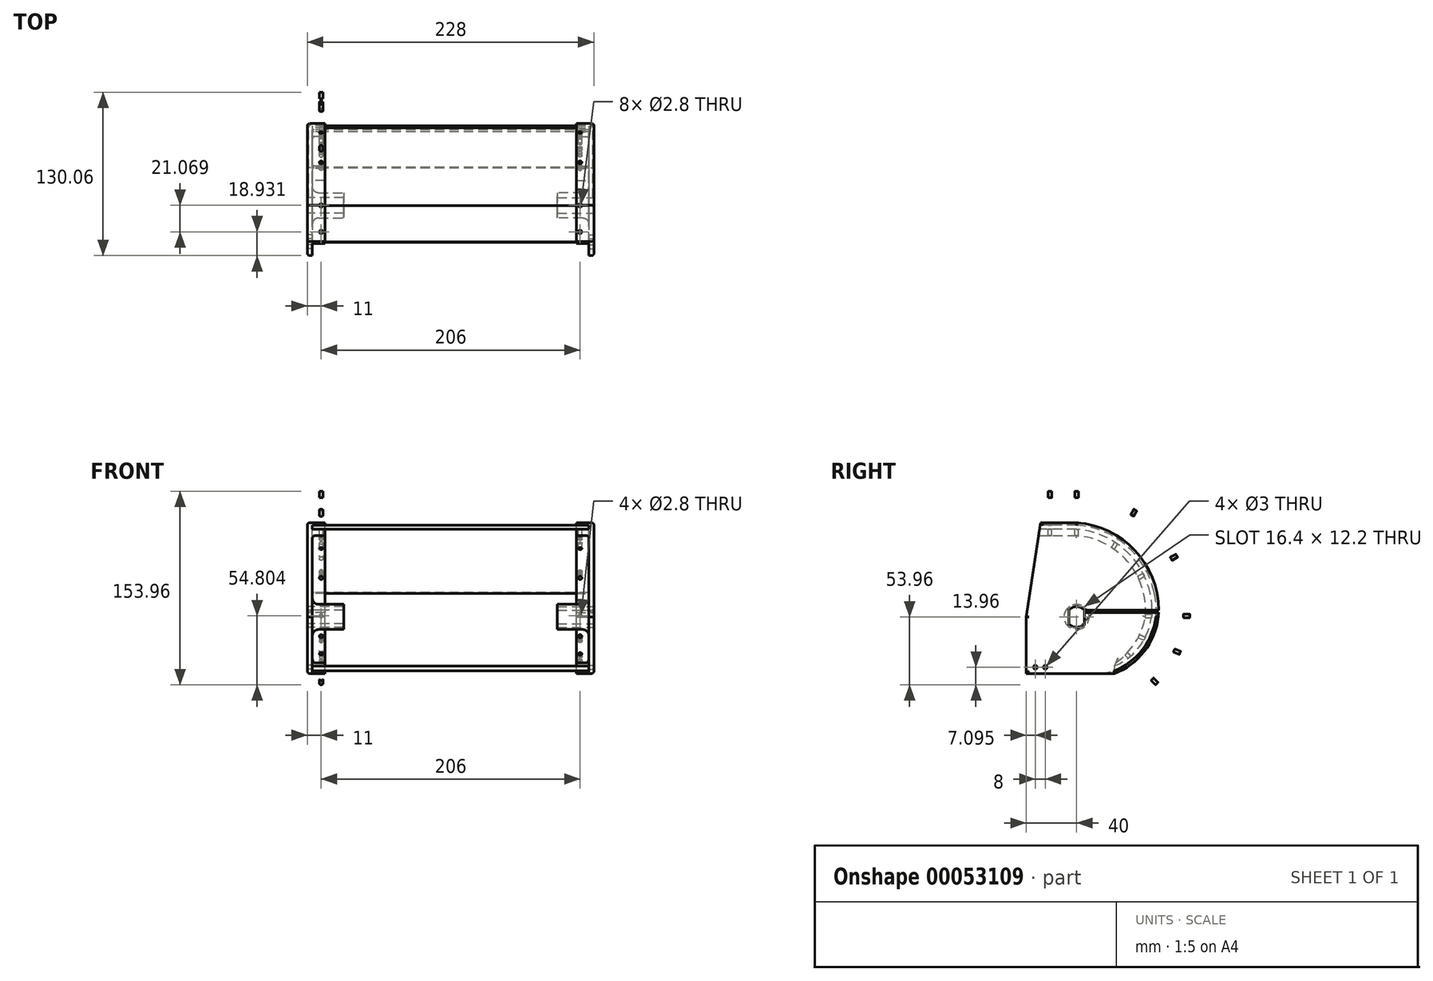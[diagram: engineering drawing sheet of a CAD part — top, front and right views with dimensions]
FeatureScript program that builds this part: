
annotation { "Feature Type Name" : "Feature", "Feature Type Description" : "" }
export const myFeature = defineFeature(function(context is Context, id is Id, definition is map)
    precondition{}
    {
        {
            var Q0;
            Q0=qCreatedBy(makeId("Right.planeOp"),FACE);
            var sketch = newSketch(context, id + "F0", { "sketchPlane" : qUnion([Q0])});
            skCircle(sketch, "E0", {"center": v(0, 0) * mm, "radius": 40 * mm});
            skCircle(sketch, "E1", {"center": v(0, 0) * mm, "radius": 8.2 * mm});
            skLineSegment(sketch, "E2", {"start": v(-6.1, 5.48) * mm, "end": v(-6.1, -5.48) * mm});
            skLineSegment(sketch, "E3", {"start": v(6.1, -5.48) * mm, "end": v(6.1, 5.48) * mm});
            skLineSegment(sketch, "E4", {"start": v(0, 0) * mm, "end": v(0, -45) * mm, "construction": true});
            skLineSegment(sketch, "E5", {"start": v(0, 0) * mm, "end": v(65, 0) * mm, "construction": true});
            skLineSegment(sketch, "E6", {"start": v(0, 0) * mm, "end": v(0, 75) * mm, "construction": true});
            skArc(sketch, "E7", {"start": v(65, 0) * mm, "mid": v(48.17, 51.08) * mm, "end": v(0, 75) * mm});
            skLineSegment(sketch, "E8", {"start": v(0, -45) * mm, "end": v(30, -45) * mm});
            skArc(sketch, "E9", {"start": v(30, -45) * mm, "mid": v(53.79, -27.4) * mm, "end": v(65, 0) * mm});
            skLineSegment(sketch, "E10", {"start": v(0, -45) * mm, "end": v(-40, -45) * mm});
            skLineSegment(sketch, "E11", {"start": v(-40, -45) * mm, "end": v(-40, 0) * mm});
            skLineSegment(sketch, "E12", {"start": v(-28.66, 75) * mm, "end": v(0, 75) * mm});
            skLineSegment(sketch, "E13", {"start": v(-40, 0) * mm, "end": v(-28.66, 75) * mm});
            skLineSegment(sketch, "E14.0", {"start": v(-28.96, 73) * mm, "end": v(-0.07, 73) * mm});
            skArc(sketch, "E14.1", {"start": v(61.76, 19.33) * mm, "mid": v(39.87, 56.56) * mm, "end": v(-0.07, 73) * mm});
            skArc(sketch, "E14.2", {"start": v(29.5, -43.05) * mm, "mid": v(57.45, -17.97) * mm, "end": v(61.76, 19.33) * mm});
            skArc(sketch, "E15.0", {"start": v(20.83, -42.2) * mm, "mid": v(52.6, -19.83) * mm, "end": v(58.54, 18.58) * mm});
            skArc(sketch, "E15.1", {"start": v(58.54, 18.58) * mm, "mid": v(37.77, 54) * mm, "end": v(-0.18, 69.7) * mm});
            skLineSegment(sketch, "E15.2", {"start": v(-29.46, 69.7) * mm, "end": v(-0.18, 69.7) * mm});
            skArc(sketch, "E16.1", {"start": v(54.69, 0.26) * mm, "mid": v(40.66, 44) * mm, "end": v(-0.35, 64.7) * mm});
            skLineSegment(sketch, "E16.2", {"start": v(-30.22, 64.7) * mm, "end": v(-0.35, 64.7) * mm});
            skLineSegment(sketch, "E17", {"start": v(29.5, -43.05) * mm, "end": v(19.71, -45) * mm});
            skLineSegment(sketch, "E18", {"start": v(20.86, -42.37) * mm, "end": v(20.83, -42.2) * mm});
            skArc(sketch, "E19", {"start": v(20.86, -42.37) * mm, "mid": v(43.09, -25.27) * mm, "end": v(54.69, 0.26) * mm});
            skLineSegment(sketch, "E20", {"start": v(30.2, -39.2) * mm, "end": v(31.32, -36.44) * mm});
            skPoint(sketch, "E21", {"position": v(-32.9, -40) * mm});
            skPoint(sketch, "E22", {"position": v(-24.9, -40) * mm});
            skCircle(sketch, "E23", {"center": v(-32.9, -40) * mm, "radius": 1.5 * mm});
            skCircle(sketch, "E24", {"center": v(-24.9, -40) * mm, "radius": 1.5 * mm});
            skSolve(sketch);
        }
        {
            var Q0;
            Q0=makeQuery(id+"F0.imprint","IMPRINT",FACE,{"disambiguationData":[TD([[makeQuery(id+"F0.imprint","IMPRINT",EDGE,{"derivedFrom":sQuery(id+"F0.wireOp",EDGE,"E7")}),1.0]])]});
            var Q1;
            {var subQ4=sQuery(id+"F0.wireOp",EDGE,"E1");var subQ8=sQuery(id+"F0.wireOp",EDGE,"E2");var subQ9=makeQuery(id+"F0.imprint","INTERSECT",VERTEX,{"disambiguationData":[OD(0.0)],"derivedFrom":[subQ4,subQ8]});Q1=makeQuery(id+"F0.imprint","IMPRINT",FACE,{"disambiguationData":[TD([[makeQuery(id+"F0.imprint","IMPRINT",EDGE,{"disambiguationData":[TD([[subQ9,1.0]])],"derivedFrom":subQ4}),-1.0]])]});}
            var Q2;
            {var subQ0=sQuery(id+"F0.wireOp",EDGE,"E2");Q2=makeQuery(id+"F0.imprint","IMPRINT",FACE,{"disambiguationData":[TD([[makeQuery(id+"F0.imprint","IMPRINT",EDGE,{"derivedFrom":subQ0}),-1.0]])]});}
            var Q3;
            {var subQ0=sQuery(id+"F0.wireOp",EDGE,"E3");Q3=makeQuery(id+"F0.imprint","IMPRINT",FACE,{"disambiguationData":[TD([[makeQuery(id+"F0.imprint","IMPRINT",EDGE,{"derivedFrom":subQ0}),-1.0]])]});}
            var Q4;
            {var subQ12=sQuery(id+"F0.wireOp",EDGE,"E10");Q4=makeQuery(id+"F0.imprint","IMPRINT",FACE,{"disambiguationData":[TD([[makeQuery(id+"F0.imprint","IMPRINT",EDGE,{"derivedFrom":subQ12}),-1.0]])]});}
            var Q5;
            {var subQ4=sQuery(id+"F0.wireOp",EDGE,"E15.0");Q5=makeQuery(id+"F0.imprint","IMPRINT",FACE,{"disambiguationData":[TD([[makeQuery(id+"F0.imprint","IMPRINT",EDGE,{"derivedFrom":subQ4}),1.0]])]});}
            var Q6;
            {var subQ4=sQuery(id+"F0.wireOp",EDGE,"E14.0");Q6=makeQuery(id+"F0.imprint","IMPRINT",FACE,{"disambiguationData":[TD([[makeQuery(id+"F0.imprint","IMPRINT",EDGE,{"derivedFrom":subQ4}),-1.0]])]});}
            var Q7;
            {var subQ0=sQuery(id+"F0.wireOp",EDGE,"E18");Q7=makeQuery(id+"F0.imprint","IMPRINT",FACE,{"disambiguationData":[TD([[makeQuery(id+"F0.imprint","IMPRINT",EDGE,{"derivedFrom":subQ0}),1.0]])]});}
            var Q8;
            {var subQ7=sQuery(id+"F0.wireOp",EDGE,"E15.1");Q8=makeQuery(id+"F0.imprint","IMPRINT",FACE,{"disambiguationData":[TD([[makeQuery(id+"F0.imprint","IMPRINT",EDGE,{"derivedFrom":subQ7}),1.0]])]});}
            var Q9;
            {var subQ0=sQuery(id+"F0.wireOp",EDGE,"E18");Q9=makeQuery(id+"F0.imprint","IMPRINT",FACE,{"disambiguationData":[TD([[makeQuery(id+"F0.imprint","IMPRINT",EDGE,{"derivedFrom":subQ0}),-1.0]])]});}
            var Q10;
            Q10=sQuery(id+"F0.wireOp",EDGE,"E12");
            var Q11;
            Q11=sQuery(id+"F0.wireOp",EDGE,"E13");
            var Q12;
            Q12=sQuery(id+"F0.wireOp",EDGE,"E11");
            var Q13;
            Q13=sQuery(id+"F0.wireOp",EDGE,"E10");
            var Q14;
            Q14=sQuery(id+"F0.wireOp",EDGE,"E8");
            var Q15;
            Q15=sQuery(id+"F0.wireOp",EDGE,"E9");
            var Q16;
            Q16=sQuery(id+"F0.wireOp",EDGE,"E7");
            extrude(context, id + "F1", {"entities" : qUnion([Q0, Q1, Q2, Q3, Q4, Q5, Q6, Q7, Q8, Q9]), "surfaceEntities" : qUnion([Q10, Q11, Q12, Q13, Q14, Q15, Q16]), "depth" : 29 * mm});
        }
        {
            var Q0;
            Q0=makeQuery(id+"F1.opExtrude","CAP_FACE",FACE,{"disambiguationData":[OSD([sQuery(id+"F0.wireOp",EDGE,"E1"),sQuery(id+"F0.wireOp",EDGE,"E2"),sQuery(id+"F0.wireOp",EDGE,"E3"),sQuery(id+"F0.wireOp",EDGE,"E7"),sQuery(id+"F0.wireOp",EDGE,"E8"),sQuery(id+"F0.wireOp",EDGE,"E9"),sQuery(id+"F0.wireOp",EDGE,"E10"),sQuery(id+"F0.wireOp",EDGE,"E11"),sQuery(id+"F0.wireOp",EDGE,"E12"),sQuery(id+"F0.wireOp",EDGE,"E13"),sQuery(id+"F0.wireOp",EDGE,"b91848d7-33e1-4d5c-aaae-2f8c404cd7a8"),sQuery(id+"F0.wireOp",EDGE,"291409aa-1abd-44d4-8dab-fd7a7754a467")])],"isStart":false});
            var sketch = newSketch(context, id + "F2", { "sketchPlane" : qUnion([Q0])});
            skCircle(sketch, "E25", {"center": v(0, 0) * mm, "radius": 10 * mm});
            skSolve(sketch);
        }
        {
            var Q0;
            {var subQ1=sQuery(id+"F0.wireOp",EDGE,"E2");Q0=makeQuery(id+"F2.imprint","IMPRINT",FACE,{"disambiguationData":[TD([[makeQuery(id+"F2.imprint","IMPRINT",EDGE,{"derivedFrom":makeQuery(id+"F1.opExtrude","CAP_EDGE",EDGE,{"disambiguationData":[OSD([subQ1])],"isStart":true})}),-1.0]])]});}
            var Q1;
            Q1=makeQuery(id+"F2.imprint","IMPRINT",FACE,{"disambiguationData":[TD([[makeQuery(id+"F2.imprint","IMPRINT",EDGE,{"derivedFrom":sQuery(id+"F2.wireOp",EDGE,"E25")}),-1.0]])]});
            extrude(context, id + "F3", {"entities" : qUnion([Q0, Q1]), "operationType" : NewBodyOperationType.REMOVE, "oppositeDirection" : true, "depth" : 25 * mm});
        }
        {
            var Q0;
            {var subQ7=sQuery(id+"F0.wireOp",EDGE,"E15.1");Q0=makeQuery(id+"F0.imprint","IMPRINT",FACE,{"disambiguationData":[TD([[makeQuery(id+"F0.imprint","IMPRINT",EDGE,{"derivedFrom":subQ7}),1.0]])]});}
            extrude(context, id + "F4", {"entities" : qUnion([Q0]), "operationType" : NewBodyOperationType.ADD, "depth" : 10 * mm});
        }
        {
            var Q0;
            Q0=makeQuery(id+"F0.imprint","IMPRINT",FACE,{"disambiguationData":[TD([[makeQuery(id+"F0.imprint","IMPRINT",EDGE,{"derivedFrom":sQuery(id+"F0.wireOp",EDGE,"E7")}),1.0]])]});
            extrude(context, id + "F5", {"entities" : qUnion([Q0]), "operationType" : NewBodyOperationType.ADD, "depth" : 10 * mm});
        }
        {
            var Q0;
            Q0=makeQuery(id+"F3.boolean.opBoolean","COPY",EDGE,{"derivedFrom":makeQuery(id+"F3.opExtrude","CAP_EDGE",EDGE,{"disambiguationData":[OSD([sQuery(id+"F2.wireOp",EDGE,"E25")])],"isStart":false})});
            fillet(context, id + "F6", {"entities" : qUnion([Q0]), "radius" : 5 * mm, "tangentPropagation" : true, "allowEdgeOverflow" : false});
        }
        {
            var Q0;
            Q0=makeQuery(id+"F3.boolean.opBoolean","COPY",EDGE,{"derivedFrom":makeQuery(id+"F3.opExtrude","CAP_EDGE",EDGE,{"disambiguationData":[OSD([sQuery(id+"F2.wireOp",EDGE,"E25")])],"isStart":true})});
            var Q1;
            Q1=makeQuery(id+"F4.boolean.opBoolean","INTERSECT",EDGE,{"derivedFrom":[makeQuery(id+"F3.boolean.opBoolean","COPY",FACE,{"derivedFrom":makeQuery(id+"F3.opExtrude","CAP_FACE",FACE,{"disambiguationData":[OSD([sQuery(id+"F0.wireOp",EDGE,"E7"),sQuery(id+"F0.wireOp",EDGE,"E8"),sQuery(id+"F0.wireOp",EDGE,"E9"),sQuery(id+"F0.wireOp",EDGE,"E10"),sQuery(id+"F0.wireOp",EDGE,"E11"),sQuery(id+"F0.wireOp",EDGE,"E12"),sQuery(id+"F0.wireOp",EDGE,"E13"),sQuery(id+"F2.wireOp",EDGE,"E25")])],"isStart":false})}),makeQuery(id+"F4.opExtrude","SWEPT_FACE",FACE,{"disambiguationData":[OSD([sQuery(id+"F0.wireOp",EDGE,"E19")])]})]});
            var Q2;
            Q2=makeQuery(id+"F4.boolean.opBoolean","INTERSECT",EDGE,{"derivedFrom":[makeQuery(id+"F3.boolean.opBoolean","COPY",FACE,{"derivedFrom":makeQuery(id+"F3.opExtrude","CAP_FACE",FACE,{"disambiguationData":[OSD([sQuery(id+"F0.wireOp",EDGE,"E7"),sQuery(id+"F0.wireOp",EDGE,"E8"),sQuery(id+"F0.wireOp",EDGE,"E9"),sQuery(id+"F0.wireOp",EDGE,"E10"),sQuery(id+"F0.wireOp",EDGE,"E11"),sQuery(id+"F0.wireOp",EDGE,"E12"),sQuery(id+"F0.wireOp",EDGE,"E13"),sQuery(id+"F2.wireOp",EDGE,"E25")])],"isStart":false})}),makeQuery(id+"F4.opExtrude","SWEPT_FACE",FACE,{"disambiguationData":[OSD([sQuery(id+"F0.wireOp",EDGE,"E16.1")])]})]});
            var Q3;
            Q3=makeQuery(id+"F4.boolean.opBoolean","INTERSECT",EDGE,{"derivedFrom":[makeQuery(id+"F3.boolean.opBoolean","COPY",FACE,{"derivedFrom":makeQuery(id+"F3.opExtrude","CAP_FACE",FACE,{"disambiguationData":[OSD([sQuery(id+"F0.wireOp",EDGE,"E7"),sQuery(id+"F0.wireOp",EDGE,"E8"),sQuery(id+"F0.wireOp",EDGE,"E9"),sQuery(id+"F0.wireOp",EDGE,"E10"),sQuery(id+"F0.wireOp",EDGE,"E11"),sQuery(id+"F0.wireOp",EDGE,"E12"),sQuery(id+"F0.wireOp",EDGE,"E13"),sQuery(id+"F2.wireOp",EDGE,"E25")])],"isStart":false})}),makeQuery(id+"F4.opExtrude","SWEPT_FACE",FACE,{"disambiguationData":[OSD([sQuery(id+"F0.wireOp",EDGE,"E16.2")])]})]});
            var Q4;
            {var subQ0=sQuery(id+"F0.wireOp",EDGE,"E13");var subQ1=sQuery(id+"F0.wireOp",EDGE,"E11");Q4=makeQuery(id+"F4.boolean.opBoolean","SPLIT",EDGE,{"disambiguationData":[TD([makeQuery(id+"F1.opExtrude","SWEPT_FACE",FACE,{"disambiguationData":[OSD([subQ1])]})])],"derivedFrom":makeQuery(id+"F3.boolean.opBoolean","COPY",EDGE,{"derivedFrom":makeQuery(id+"F3.opExtrude","CAP_EDGE",EDGE,{"disambiguationData":[OSD([subQ0])],"isStart":false})})});}
            var Q5;
            Q5=makeQuery(id+"F3.boolean.opBoolean","COPY",EDGE,{"derivedFrom":makeQuery(id+"F3.opExtrude","CAP_EDGE",EDGE,{"disambiguationData":[OSD([sQuery(id+"F0.wireOp",EDGE,"E11")])],"isStart":false})});
            var Q6;
            Q6=makeQuery(id+"F3.boolean.opBoolean","COPY",EDGE,{"derivedFrom":makeQuery(id+"F3.opExtrude","CAP_EDGE",EDGE,{"disambiguationData":[OSD([sQuery(id+"F0.wireOp",EDGE,"E8"),sQuery(id+"F0.wireOp",EDGE,"E10")])],"isStart":false})});
            var Q7;
            Q7=makeQuery(id+"F1.opExtrude","CAP_EDGE",EDGE,{"disambiguationData":[OSD([sQuery(id+"F0.wireOp",EDGE,"E11")])],"isStart":true});
            var Q8;
            Q8=makeQuery(id+"F1.opExtrude","CAP_EDGE",EDGE,{"disambiguationData":[OSD([sQuery(id+"F0.wireOp",EDGE,"E13")])],"isStart":true});
            var Q9;
            Q9=makeQuery(id+"F1.opExtrude","CAP_EDGE",EDGE,{"disambiguationData":[OSD([sQuery(id+"F0.wireOp",EDGE,"E8"),sQuery(id+"F0.wireOp",EDGE,"E10")])],"isStart":true});
            var Q10;
            Q10=makeQuery(id+"F1.opExtrude","CAP_EDGE",EDGE,{"disambiguationData":[OSD([sQuery(id+"F0.wireOp",EDGE,"E9")])],"isStart":true});
            var Q11;
            Q11=makeQuery(id+"F1.opExtrude","CAP_EDGE",EDGE,{"disambiguationData":[OSD([sQuery(id+"F0.wireOp",EDGE,"E7")])],"isStart":true});
            fillet(context, id + "F7", {"entities" : qUnion([Q0, Q1, Q2, Q3, Q4, Q5, Q6, Q7, Q8, Q9, Q10, Q11]), "radius" : 2 * mm, "tangentPropagation" : true, "allowEdgeOverflow" : false});
        }
        {
            var Q0;
            Q0=makeQuery(id+"F4.opExtrude","CAP_FACE",FACE,{"disambiguationData":[OSD([sQuery(id+"F0.wireOp",EDGE,"E13"),sQuery(id+"F0.wireOp",EDGE,"E15.0"),sQuery(id+"F0.wireOp",EDGE,"E15.1"),sQuery(id+"F0.wireOp",EDGE,"E15.2"),sQuery(id+"F0.wireOp",EDGE,"E16.1"),sQuery(id+"F0.wireOp",EDGE,"E16.2"),sQuery(id+"F0.wireOp",EDGE,"E19"),sQuery(id+"F0.wireOp",EDGE,"E20")])],"isStart":false});
            var Q1;
            Q1=makeQuery(id+"F5.opExtrude","CAP_FACE",FACE,{"disambiguationData":[OSD([sQuery(id+"F0.wireOp",EDGE,"E7"),sQuery(id+"F0.wireOp",EDGE,"E8"),sQuery(id+"F0.wireOp",EDGE,"E9"),sQuery(id+"F0.wireOp",EDGE,"E12"),sQuery(id+"F0.wireOp",EDGE,"E13"),sQuery(id+"F0.wireOp",EDGE,"E14.0"),sQuery(id+"F0.wireOp",EDGE,"E14.1"),sQuery(id+"F0.wireOp",EDGE,"E14.2"),sQuery(id+"F0.wireOp",EDGE,"E17")])],"isStart":false});
            extrude(context, id + "F8", {"entities" : qUnion([Q0, Q1]), "operationType" : NewBodyOperationType.ADD, "depth" : 4 * mm});
        }
        {
            var Q0;
            {var subQ0=sQuery(id+"F0.wireOp",EDGE,"E12");Q0=makeQuery(id+"F8.boolean.opBoolean","MERGE",FACE,{"derivedFrom":[makeQuery(id+"F5.boolean.opBoolean","MERGE",FACE,{"derivedFrom":[makeQuery(id+"F1.opExtrude","SWEPT_FACE",FACE,{"disambiguationData":[OSD([subQ0])]}),makeQuery(id+"F5.opExtrude","SWEPT_FACE",FACE,{"disambiguationData":[OSD([subQ0])]})]}),makeQuery(id+"F8.opExtrude","SWEPT_FACE",FACE,{"disambiguationData":[OSD([subQ0])]})]});}
            var sketch = newSketch(context, id + "F9", { "sketchPlane" : qUnion([Q0])});
            skCircle(sketch, "E26", {"center": v(11, 0) * mm, "radius": 1.4 * mm});
            skCircle(sketch, "E27", {"center": v(11, -21.07) * mm, "radius": 1.4 * mm});
            skSolve(sketch);
        }
        {
            var Q0;
            Q0=makeQuery(id+"F9.imprint","IMPRINT",FACE,{"disambiguationData":[TD([[makeQuery(id+"F9.imprint","IMPRINT",EDGE,{"derivedFrom":sQuery(id+"F9.wireOp",EDGE,"E27")}),-1.0]])]});
            cPlane(context, id + "F10", {"entities" : qUnion([Q0]), "cplaneType" : CPlaneType.OFFSET, "offset" : 20 * mm, "width" : 150 * mm, "height" : 150 * mm});
        }
        {
            var Q0;
            Q0=qCreatedBy(id+"F10.planeOp",FACE);
            var sketch = newSketch(context, id + "F11", { "sketchPlane" : qUnion([Q0])});
            skCircle(sketch, "E28.0", {"center": v(11, 0) * mm, "radius": 1.4 * mm});
            skCircle(sketch, "E29.0", {"center": v(11, -21.07) * mm, "radius": 1.4 * mm});
            skSolve(sketch);
        }
        {
            var Q0;
            Q0=makeQuery(id+"F11.imprint","IMPRINT",FACE,{"disambiguationData":[TD([[makeQuery(id+"F11.imprint","IMPRINT",EDGE,{"derivedFrom":sQuery(id+"F11.wireOp",EDGE,"E28.0")}),1.0]])]});
            var Q1;
            Q1=makeQuery(id+"F11.imprint","IMPRINT",FACE,{"disambiguationData":[TD([[makeQuery(id+"F11.imprint","IMPRINT",EDGE,{"derivedFrom":sQuery(id+"F11.wireOp",EDGE,"E29.0")}),1.0]])]});
            extrude(context, id + "F12", {"entities" : qUnion([Q0, Q1]), "depth" : 5 * mm});
        }
        {
            var Q0;
            Q0=makeQuery(id+"F12.opExtrude","SWEPT_BODY",BODY,{"disambiguationData":[OSD([sQuery(id+"F11.wireOp",EDGE,"E28.0")])]});
            var Q1;
            {var subQ0=sQuery(id+"F0.wireOp",EDGE,"E7");Q1=makeQuery(id+"F8.boolean.opBoolean","MERGE",FACE,{"derivedFrom":[makeQuery(id+"F5.boolean.opBoolean","MERGE",FACE,{"derivedFrom":[makeQuery(id+"F1.opExtrude","SWEPT_FACE",FACE,{"disambiguationData":[OSD([subQ0])]}),makeQuery(id+"F5.opExtrude","SWEPT_FACE",FACE,{"disambiguationData":[OSD([subQ0])]})]}),makeQuery(id+"F8.opExtrude","SWEPT_FACE",FACE,{"disambiguationData":[OSD([subQ0])]})]});}
            circularPattern(context, id + "F13", {"entities" : qUnion([Q0]), "axis" : qUnion([Q1]), "angle" : 30 * degree, "instanceCount" : round(4), "computeTransformsWithoutBuiltin" : true});
        }
        {
            var Q0;
            Q0=makeQuery(id+"F13.opPattern","COPY",BODY,{"derivedFrom":makeQuery(id+"F12.opExtrude","SWEPT_BODY",BODY,{"disambiguationData":[OSD([sQuery(id+"F11.wireOp",EDGE,"E28.0")])]}),"instanceName":"3"});
            var Q1;
            {var subQ0=sQuery(id+"F0.wireOp",EDGE,"E9");Q1=makeQuery(id+"F5.boolean.opBoolean","MERGE",FACE,{"derivedFrom":[makeQuery(id+"F1.opExtrude","SWEPT_FACE",FACE,{"disambiguationData":[OSD([subQ0])]}),makeQuery(id+"F5.opExtrude","SWEPT_FACE",FACE,{"disambiguationData":[OSD([subQ0])]})]});}
            circularPattern(context, id + "F14", {"entities" : qUnion([Q0]), "axis" : qUnion([Q1]), "angle" : 22 * degree, "instanceCount" : round(3), "computeTransformsWithoutBuiltin" : true});
        }
        {
            var Q0;
            Q0=makeQuery(id+"F12.opExtrude","CAP_FACE",FACE,{"disambiguationData":[OSD([sQuery(id+"F11.wireOp",EDGE,"E29.0")])],"isStart":true});
            var Q1;
            Q1=makeQuery(id+"F12.opExtrude","CAP_FACE",FACE,{"disambiguationData":[OSD([sQuery(id+"F11.wireOp",EDGE,"E28.0")])],"isStart":true});
            extrude(context, id + "F15", {"entities" : qUnion([Q0, Q1]), "operationType" : NewBodyOperationType.REMOVE, "depth" : 40 * mm});
        }
        {
            var Q0;
            Q0=makeQuery(id+"F13.opPattern","COPY",FACE,{"derivedFrom":makeQuery(id+"F12.opExtrude","CAP_FACE",FACE,{"disambiguationData":[OSD([sQuery(id+"F11.wireOp",EDGE,"E28.0")])],"isStart":true}),"instanceName":"1"});
            extrude(context, id + "F16", {"entities" : qUnion([Q0]), "operationType" : NewBodyOperationType.REMOVE, "depth" : 40 * mm});
        }
        {
            var Q0;
            Q0=makeQuery(id+"F13.opPattern","COPY",FACE,{"derivedFrom":makeQuery(id+"F12.opExtrude","CAP_FACE",FACE,{"disambiguationData":[OSD([sQuery(id+"F11.wireOp",EDGE,"E28.0")])],"isStart":true}),"instanceName":"2"});
            extrude(context, id + "F17", {"entities" : qUnion([Q0]), "operationType" : NewBodyOperationType.REMOVE, "depth" : 40 * mm});
        }
        {
            var Q0;
            Q0=makeQuery(id+"F13.opPattern","COPY",FACE,{"derivedFrom":makeQuery(id+"F12.opExtrude","CAP_FACE",FACE,{"disambiguationData":[OSD([sQuery(id+"F11.wireOp",EDGE,"E28.0")])],"isStart":true}),"instanceName":"3"});
            extrude(context, id + "F18", {"entities" : qUnion([Q0]), "operationType" : NewBodyOperationType.REMOVE, "depth" : 40 * mm});
        }
        {
            var Q0;
            Q0=makeQuery(id+"F14.opPattern","COPY",FACE,{"derivedFrom":makeQuery(id+"F13.opPattern","COPY",FACE,{"derivedFrom":makeQuery(id+"F12.opExtrude","CAP_FACE",FACE,{"disambiguationData":[OSD([sQuery(id+"F11.wireOp",EDGE,"E28.0")])],"isStart":true}),"instanceName":"3"}),"instanceName":"1"});
            extrude(context, id + "F19", {"entities" : qUnion([Q0]), "operationType" : NewBodyOperationType.REMOVE, "depth" : 40 * mm});
        }
        {
            var Q0;
            Q0=makeQuery(id+"F14.opPattern","COPY",FACE,{"derivedFrom":makeQuery(id+"F13.opPattern","COPY",FACE,{"derivedFrom":makeQuery(id+"F12.opExtrude","CAP_FACE",FACE,{"disambiguationData":[OSD([sQuery(id+"F11.wireOp",EDGE,"E28.0")])],"isStart":true}),"instanceName":"3"}),"instanceName":"2"});
            extrude(context, id + "F20", {"entities" : qUnion([Q0]), "operationType" : NewBodyOperationType.REMOVE, "depth" : 40 * mm});
        }
        {
            var Q0;
            Q0=makeQuery(id+"F1.opExtrude","CAP_EDGE",EDGE,{"disambiguationData":[OSD([sQuery(id+"F0.wireOp",EDGE,"E3")])],"isStart":true});
            var Q1;
            {var subQ0=sQuery(id+"F0.wireOp",EDGE,"E1");Q1=makeQuery(id+"F1.opExtrude","CAP_EDGE",EDGE,{"disambiguationData":[OSD([subQ0]),TDD([makeQuery(id+"F0.imprint","IMPRINT",EDGE,{"disambiguationData":[TD([[makeQuery(id+"F0.imprint","INTERSECT",VERTEX,{"disambiguationData":[OD(0.0)],"derivedFrom":[subQ0,sQuery(id+"F0.wireOp",EDGE,"E2")]}),1.0]])],"derivedFrom":subQ0})])],"isStart":true});}
            var Q2;
            Q2=makeQuery(id+"F1.opExtrude","CAP_EDGE",EDGE,{"disambiguationData":[OSD([sQuery(id+"F0.wireOp",EDGE,"E2")])],"isStart":true});
            var Q3;
            {var subQ0=sQuery(id+"F0.wireOp",EDGE,"E1");Q3=makeQuery(id+"F1.opExtrude","CAP_EDGE",EDGE,{"disambiguationData":[OSD([subQ0]),TDD([makeQuery(id+"F0.imprint","IMPRINT",EDGE,{"disambiguationData":[TD([[makeQuery(id+"F0.imprint","INTERSECT",VERTEX,{"disambiguationData":[OD(1.0)],"derivedFrom":[subQ0,sQuery(id+"F0.wireOp",EDGE,"E2")]}),-1.0]])],"derivedFrom":subQ0})])],"isStart":true});}
            fillet(context, id + "F21", {"entities" : qUnion([Q0, Q1, Q2, Q3]), "radius" : 1 * mm, "tangentPropagation" : true, "allowEdgeOverflow" : false});
        }
        {
            var Q0;
            Q0=makeQuery(id+"F1.opExtrude","CAP_FACE",FACE,{"disambiguationData":[OSD([sQuery(id+"F0.wireOp",EDGE,"E1"),sQuery(id+"F0.wireOp",EDGE,"E2"),sQuery(id+"F0.wireOp",EDGE,"E3"),sQuery(id+"F0.wireOp",EDGE,"E7"),sQuery(id+"F0.wireOp",EDGE,"E8"),sQuery(id+"F0.wireOp",EDGE,"E9"),sQuery(id+"F0.wireOp",EDGE,"E10"),sQuery(id+"F0.wireOp",EDGE,"E11"),sQuery(id+"F0.wireOp",EDGE,"E12"),sQuery(id+"F0.wireOp",EDGE,"E13"),sQuery(id+"F0.wireOp",EDGE,"E23"),sQuery(id+"F0.wireOp",EDGE,"E24")])],"isStart":true});
            var sketch = newSketch(context, id + "F22", { "sketchPlane" : qUnion([Q0])});
            skCircle(sketch, "E30", {"center": v(-65.2, 4.44) * mm, "radius": 1 * mm});
            skArc(sketch, "E31.0", {"start": v(-30, -45) * mm, "mid": v(-53.79, -27.4) * mm, "end": v(-65, 0) * mm});
            skArc(sketch, "E32.0", {"start": v(-65, 0) * mm, "mid": v(-48.17, 51.08) * mm, "end": v(0, 75) * mm});
            skLineSegment(sketch, "E33", {"start": v(-65.2, 4.44) * mm, "end": v(-3.8, 4.44) * mm});
            skCircle(sketch, "E34", {"center": v(-65.2, 4.44) * mm, "radius": 1.5 * mm});
            skLineSegment(sketch, "E35", {"start": v(-65.6, 5.36) * mm, "end": v(-65.84, 5.81) * mm});
            skSolve(sketch);
        }
        {
            var Q0;
            {var subQ0=sQuery(id+"F22.wireOp",EDGE,"E33");var subQ1=sQuery(id+"F22.wireOp",EDGE,"E30");var subQ2=makeQuery(id+"F22.imprint","INTERSECT",VERTEX,{"derivedFrom":[subQ1,subQ0]});Q0=makeQuery(id+"F22.imprint","IMPRINT",FACE,{"disambiguationData":[TD([[makeQuery(id+"F22.imprint","IMPRINT",EDGE,{"disambiguationData":[TD([[subQ2,1.0]])],"derivedFrom":subQ1}),1.0]])]});}
            var Q1;
            {var subQ0=sQuery(id+"F22.wireOp",EDGE,"E32.0");var subQ1=sQuery(id+"F22.wireOp",EDGE,"E30");var subQ2=makeQuery(id+"F22.imprint","INTERSECT",VERTEX,{"disambiguationData":[OD(0.0)],"derivedFrom":[subQ1,subQ0]});Q1=makeQuery(id+"F22.imprint","IMPRINT",FACE,{"disambiguationData":[TD([[makeQuery(id+"F22.imprint","IMPRINT",EDGE,{"disambiguationData":[TD([[subQ2,1.0]])],"derivedFrom":subQ1}),1.0]])]});}
            extrude(context, id + "F23", {"entities" : qUnion([Q0, Q1]), "operationType" : NewBodyOperationType.REMOVE, "oppositeDirection" : true, "depth" : 25 * mm});
        }
        {
            var Q0;
            Q0=qCreatedBy(makeId("Front.planeOp"),FACE);
            cPlane(context, id + "F24", {"entities" : qUnion([Q0]), "cplaneType" : CPlaneType.OFFSET, "offset" : 65 * mm, "oppositeDirection" : true, "width" : 150 * mm, "height" : 150 * mm});
        }
        {
            var Q0;
            Q0=qCreatedBy(id+"F24.planeOp",FACE);
            var sketch = newSketch(context, id + "F25", { "sketchPlane" : qUnion([Q0])});
            skFitSpline(sketch, "E36.0", {"points": [v(2, 3.44) * mm, v(1.7, 3.44) * mm, v(1.48, 3.45) * mm, v(1.36, 3.45) * mm, v(1.25, 3.46) * mm, v(1.15, 3.47) * mm, v(1.07, 3.48) * mm, v(0.96, 3.5) * mm, v(0.87, 3.51) * mm, v(0.8, 3.54) * mm, v(0.7, 3.57) * mm, v(0.61, 3.62) * mm, v(0.54, 3.68) * mm, v(0.47, 3.75) * mm, v(0.4, 3.83) * mm, v(0.36, 3.93) * mm, v(0.33, 4) * mm, v(0.3, 4.09) * mm, v(0.3, 4.18) * mm, v(0.28, 4.27) * mm, v(0.27, 4.36) * mm, v(0.27, 4.45) * mm, v(0.27, 4.57) * mm, v(0.28, 4.67) * mm, v(0.3, 4.77) * mm, v(0.32, 4.88) * mm, v(0.35, 4.97) * mm, v(0.4, 5.05) * mm, v(0.44, 5.13) * mm, v(0.5, 5.2) * mm, v(0.57, 5.24) * mm, v(0.63, 5.3) * mm, v(0.7, 5.33) * mm, v(0.8, 5.36) * mm, v(0.87, 5.39) * mm, v(0.96, 5.4) * mm, v(1.06, 5.42) * mm, v(1.15, 5.43) * mm, v(1.24, 5.44) * mm, v(1.36, 5.44) * mm, v(1.44, 5.44) * mm, v(1.55, 5.44) * mm, v(1.68, 5.44) * mm, v(1.71, 5.44) * mm, v(1.82, 5.44) * mm, v(2, 5.44) * mm]});
            skLineSegment(sketch, "E37.0", {"start": v(0, 0.2) * mm, "end": v(0, 73) * mm});
            skLineSegment(sketch, "E38", {"start": v(0.27, 4.45) * mm, "end": v(0, 4.45) * mm});
            skCircle(sketch, "E39", {"center": v(0, 4.45) * mm, "radius": 1 * mm});
            skSolve(sketch);
        }
        {
            var Q0;
            {var subQ0=sQuery(id+"F25.wireOp",EDGE,"E38");Q0=makeQuery(id+"F25.imprint","IMPRINT",FACE,{"disambiguationData":[TD([[makeQuery(id+"F25.imprint","IMPRINT",EDGE,{"derivedFrom":subQ0}),1.0]])]});}
            var Q1;
            {var subQ0=sQuery(id+"F25.wireOp",EDGE,"E36.0");var subQ3=makeQuery(id+"F25.imprint","INTERSECT",VERTEX,{"derivedFrom":[subQ0,sQuery(id+"F25.wireOp",EDGE,"E38")]});Q1=makeQuery(id+"F25.imprint","IMPRINT",FACE,{"disambiguationData":[TD([[makeQuery(id+"F25.imprint","IMPRINT",EDGE,{"disambiguationData":[TD([[subQ3,1.0]])],"derivedFrom":subQ0}),-1.0]])]});}
            var Q2;
            {var subQ5=sQuery(id+"F25.wireOp",EDGE,"E38");Q2=makeQuery(id+"F25.imprint","IMPRINT",FACE,{"disambiguationData":[TD([[makeQuery(id+"F25.imprint","IMPRINT",EDGE,{"derivedFrom":subQ5}),-1.0]])]});}
            var Q3;
            Q3=qCreatedBy(makeId("Front.planeOp"),FACE);
            extrude(context, id + "F26", {"entities" : qUnion([Q0, Q1, Q2]), "operationType" : NewBodyOperationType.REMOVE, "endBound" : BoundingType.UP_TO_SURFACE, "endBoundEntityFace" : qUnion([Q3]), "depth" : 25 * mm});
        }
        {
            var Q0;
            Q0=makeQuery(id+"F26.boolean.opBoolean","INTERSECT",EDGE,{"derivedFrom":[makeQuery(id+"F23.boolean.opBoolean","COPY",FACE,{"derivedFrom":makeQuery(id+"F23.opExtrude","SWEPT_FACE",FACE,{"disambiguationData":[OSD([sQuery(id+"F22.wireOp",EDGE,"E30")])]})}),makeQuery(id+"F26.opExtrude","SWEPT_FACE",FACE,{"disambiguationData":[OSD([sQuery(id+"F25.wireOp",EDGE,"E39")])]})]});
            fillet(context, id + "F27", {"entities" : qUnion([Q0]), "radius" : 2 * mm, "tangentPropagation" : true, "allowEdgeOverflow" : false});
        }
        {
            var Q0;
            Q0=makeQuery(id+"F3.boolean.opBoolean","COPY",FACE,{"derivedFrom":makeQuery(id+"F3.opExtrude","CAP_FACE",FACE,{"disambiguationData":[OSD([sQuery(id+"F0.wireOp",EDGE,"E7"),sQuery(id+"F0.wireOp",EDGE,"E8"),sQuery(id+"F0.wireOp",EDGE,"E9"),sQuery(id+"F0.wireOp",EDGE,"E10"),sQuery(id+"F0.wireOp",EDGE,"E11"),sQuery(id+"F0.wireOp",EDGE,"E12"),sQuery(id+"F0.wireOp",EDGE,"E13"),sQuery(id+"F0.wireOp",EDGE,"E23"),sQuery(id+"F0.wireOp",EDGE,"E24"),sQuery(id+"F2.wireOp",EDGE,"E25")])],"isStart":false})});
            var sketch = newSketch(context, id + "F28", { "sketchPlane" : qUnion([Q0])});
            skLineSegment(sketch, "E40", {"start": v(30.2, -39.2) * mm, "end": v(29.63, -43) * mm});
            skSolve(sketch);
        }
        {
            var Q0;
            Q0=makeQuery(id+"F28.imprint","IMPRINT",FACE,{"disambiguationData":[TD([[makeQuery(id+"F28.imprint","IMPRINT",EDGE,{"derivedFrom":sQuery(id+"F28.wireOp",EDGE,"E40")}),1.0]])]});
            extrude(context, id + "F29", {"entities" : qUnion([Q0]), "depth" : 220 * mm});
        }
        {
            var Q0;
            Q0=makeQuery(id+"F29.opExtrude","CAP_FACE",FACE,{"disambiguationData":[OSD([sQuery(id+"F0.wireOp",EDGE,"E7"),sQuery(id+"F0.wireOp",EDGE,"E8"),sQuery(id+"F0.wireOp",EDGE,"E9"),sQuery(id+"F0.wireOp",EDGE,"E10"),sQuery(id+"F0.wireOp",EDGE,"E11"),sQuery(id+"F0.wireOp",EDGE,"E12"),sQuery(id+"F0.wireOp",EDGE,"E13"),sQuery(id+"F0.wireOp",EDGE,"E14.0"),sQuery(id+"F0.wireOp",EDGE,"E14.1"),sQuery(id+"F0.wireOp",EDGE,"E14.2"),sQuery(id+"F0.wireOp",EDGE,"E15.0"),sQuery(id+"F0.wireOp",EDGE,"E15.1"),sQuery(id+"F0.wireOp",EDGE,"E15.2"),sQuery(id+"F0.wireOp",EDGE,"E23"),sQuery(id+"F0.wireOp",EDGE,"E24"),sQuery(id+"F2.wireOp",EDGE,"E25"),sQuery(id+"F28.wireOp",EDGE,"E40")])],"isStart":false});
            var Q1;
            Q1=makeQuery(id+"F29.opExtrude","CAP_VERTEX",VERTEX,{"disambiguationData":[OSD([sQuery(id+"F0.wireOp",EDGE,"E7"),sQuery(id+"F0.wireOp",EDGE,"E8"),sQuery(id+"F0.wireOp",EDGE,"E9"),sQuery(id+"F0.wireOp",EDGE,"E10"),sQuery(id+"F0.wireOp",EDGE,"E11"),sQuery(id+"F0.wireOp",EDGE,"E12"),sQuery(id+"F0.wireOp",EDGE,"E13"),sQuery(id+"F0.wireOp",EDGE,"E15.0"),sQuery(id+"F0.wireOp",EDGE,"E15.1"),sQuery(id+"F0.wireOp",EDGE,"E23"),sQuery(id+"F0.wireOp",EDGE,"E24"),sQuery(id+"F2.wireOp",EDGE,"E25")])],"isStart":false});
            cPlane(context, id + "F30", {"entities" : qUnion([Q0, Q1]), "cplaneType" : CPlaneType.PLANE_POINT, "offset" : 150 * mm, "width" : 150 * mm, "height" : 150 * mm});
        }
        {
            var Q0;
            Q0=qCreatedBy(id+"F30.planeOp",FACE);
            var Q1;
            Q1=makeQuery(id+"F3.boolean.opBoolean","COPY",FACE,{"derivedFrom":makeQuery(id+"F3.opExtrude","CAP_FACE",FACE,{"disambiguationData":[OSD([sQuery(id+"F0.wireOp",EDGE,"E7"),sQuery(id+"F0.wireOp",EDGE,"E8"),sQuery(id+"F0.wireOp",EDGE,"E9"),sQuery(id+"F0.wireOp",EDGE,"E10"),sQuery(id+"F0.wireOp",EDGE,"E11"),sQuery(id+"F0.wireOp",EDGE,"E12"),sQuery(id+"F0.wireOp",EDGE,"E13"),sQuery(id+"F0.wireOp",EDGE,"E23"),sQuery(id+"F0.wireOp",EDGE,"E24"),sQuery(id+"F2.wireOp",EDGE,"E25")])],"isStart":false})});
            cPlane(context, id + "F31", {"entities" : qUnion([Q0, Q1]), "cplaneType" : CPlaneType.MID_PLANE, "offset" : 150 * mm, "width" : 150 * mm, "height" : 150 * mm});
        }
        {
            var Q0;
            Q0=makeQuery(id+"F1.opExtrude","SWEPT_BODY",BODY,{"disambiguationData":[OSD([sQuery(id+"F0.wireOp",EDGE,"E1"),sQuery(id+"F0.wireOp",EDGE,"E2"),sQuery(id+"F0.wireOp",EDGE,"E3"),sQuery(id+"F0.wireOp",EDGE,"E7"),sQuery(id+"F0.wireOp",EDGE,"E8"),sQuery(id+"F0.wireOp",EDGE,"E9"),sQuery(id+"F0.wireOp",EDGE,"E10"),sQuery(id+"F0.wireOp",EDGE,"E11"),sQuery(id+"F0.wireOp",EDGE,"E12"),sQuery(id+"F0.wireOp",EDGE,"E13"),sQuery(id+"F0.wireOp",EDGE,"E23"),sQuery(id+"F0.wireOp",EDGE,"E24")])]});
            var Q1;
            Q1=qCreatedBy(id+"F31.planeOp",FACE);
            mirror(context, id + "F32", {"entities" : qUnion([Q0]), "mirrorPlane" : qUnion([Q1])});
        }
    });
